# Revit family: RAPID25P
name_source: partatom
category: Generic Models
revit_build: Autodesk Revit LT 2017 (Build: 20170118_1100(x64)
units: mm (PartAtom-declared; Revit-internal decimal feet)

## family parameters
Always vertical = No
Can host rebar = No
Cut with Voids When Loaded = No
Part Type = Normal
Room Calculation Point = No
Round Connector Dimension = Use Diameter
Shared = No
Work Plane-Based = Yes

## types (1)
- NBS Standard Parameters
    AssetType = Fixed
    BIMObjectName = Metpro_Metprolibrary_Conduitfittings_Metalcomponent_Steelaccessories
    CodePerformance = Grey
    Default Elevation = 1219 mm
    Description = RAPID25P - 25mm Rapid Saddle
    DurationUnit = 1 Year
    Finish = BZP
    Manufacturer = Metpro Limited
    ManufacturerName = Metpro ltd
    ManufacturerURL = www.metpro.co.uk
    Material = Pressed Steel
    ModelNumber = RAPID25P
    ModelReference = Conduit fittings
    NBSDescription = Conduit Fittings
    NBSReference = 90-55-10/460
    Name = RAPID25 - RAPID SADDLE
    NominalHeight = 28 mm  [stored 0.0918635 ft]
    NominalLength = 57 mm  [stored 0.187008 ft]
    NominalWidth = 22 mm  [stored 0.0721785 ft]
    ProductInformation = www.metpro.co.uk/pdf/rapid25p.pdf
    Size = 25mm
    URL = www.metpro.co.uk
    Uniclass2 = Pr_65_70_11_20
    Version = 1
    WarrantyDurationUnit = 12 Months
    WarrantyGuarantorParts = 12 Months
    Weight = 0.025kg

note: [stored X ft] marks values corroborated as IEEE doubles in the binary element streams (Revit-internal decimal feet)

## geometry (parser evidence)
native form markers: Sweep x3
no freeform markers — native parametric forms only
